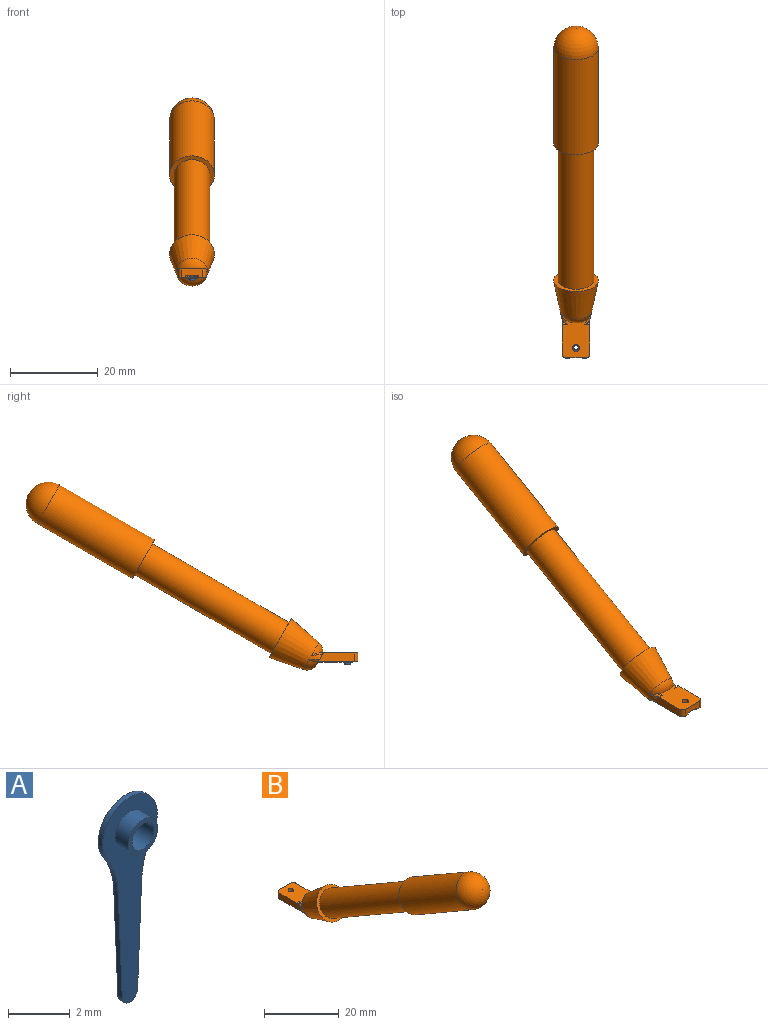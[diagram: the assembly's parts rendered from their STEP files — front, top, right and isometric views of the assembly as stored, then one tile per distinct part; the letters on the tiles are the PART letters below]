
ASSEMBLY  parts=2 mates=2
PART A: 11 faces, bbox 2.5x0.8x8.1 mm
  f0: cylinder r=0.68mm len=1.35mm, axis (0,1,0), area 2.5mm2, adj f1,f2
  f1: plane 1.35x1.35mm, normal (0,-1,0), area 0.6mm2, adj f0,f3
  f2: plane 8.1x2.5mm, normal (0,-1,0), area 8.8mm2, adj f0,f4,f5,f6,f7,f8,f9
  f3: cylinder r=0.5mm len=1mm, axis (0,-1,0), area 2.5mm2, adj f1,f10
  f4: plane 4.29x0.2mm, normal (1,0,-0.04), area 0.9mm2, adj f2,f5,f9,f10
  f5: cylinder r=3mm len=1.54mm, axis (0,-1,0), area 0.3mm2, adj f2,f4,f6,f10
  f6: cylinder r=1.25mm len=2.5mm, axis (0,-1,0), area 1.1mm2, adj f2,f5,f7,f10
  f7: cylinder r=3mm len=1.54mm, axis (0,-1,0), area 0.3mm2, adj f2,f6,f8,f10
  f8: plane 4.29x0.2mm, normal (-1,0,-0.04), area 0.9mm2, adj f2,f7,f9,f10
  f9: cylinder r=0.35mm len=0.7mm, axis (0,-1,0), area 0.2mm2, adj f2,f4,f8,f10
  f10: plane 8.1x2.5mm, normal (0,1,0), area 9.5mm2, adj f3,f4,f5,f6,f7,f8,f9
PART B: 37 faces, bbox 10.2x75.5x43.4 mm
  f0: plane 10.16x8.8mm, normal (0,-0.87,0.5), area 29.2mm2, adj f1,f6
  f1: cylinder r=4.06mm len=35.21mm, axis (0,-0.87,0.5), area 918.4mm2, adj f0,f2
  f2: plane 10.16x8.8mm, normal (0,0.87,-0.5), area 29.2mm2, adj f1,f3
  f3: cylinder r=5.08mm len=26.73mm, axis (0,-0.87,0.5), area 797.8mm2, adj f2,f28
  f4: plane 1.65x0.95mm, normal (0,-0.87,0.5), area 0.3mm2, adj f6,f24,f27,f33,f34,f35
  f5: plane 1.65x0.95mm, normal (0,-0.87,0.5), area 0.3mm2, adj f6,f22,f25,f31,f32,f36
  f6: cone r=3.17mm half-angle=10.6deg, axis (0,-0.87,0.5), area 228.7mm2, adj f0,f4,f5,f29,f30,f32,f34,f35
  f7: cylinder r=0.76mm len=1.52mm, axis (0,0,-1), area 6.7mm2, adj f14,f26
  f8: cylinder r=1.02mm len=1.91mm, axis (0,0,-1), area 2.5mm2, adj f19,f24,f26,f27
  f9: plane 2.26x0.51mm, normal (-1,0,0), area 1.1mm2, adj f10,f14,f19,f24
  f10: cylinder r=1.4mm len=0.88mm, axis (0,0,-1), area 0.5mm2, adj f9,f11,f14,f24
  f11: extruded ~1.41x0.53mm, area 0.8mm2, adj f10,f12,f14,f24
  f12: plane 4.1x0.51mm, normal (-1,0.03,0), area 2.1mm2, adj f11,f13,f14,f24
  f13: cylinder r=0.44mm len=0.51mm, axis (0,0,-1), area 0.1mm2, adj f12,f14,f23,f24
  f14: plane 8.7x2.79mm, normal (0,0,-1), area 13.2mm2, adj f7,f9,f10,f11,f12,f13,f15,f16
  f15: plane 4.1x0.51mm, normal (1,0.03,0), area 2.1mm2, adj f14,f16,f21,f22
  f16: extruded ~1.41x0.53mm, area 0.8mm2, adj f14,f15,f17,f22
  f17: cylinder r=1.4mm len=0.86mm, axis (0,0,-1), area 0.5mm2, adj f14,f16,f18,f22
  f18: plane 2.29x0.51mm, normal (1,0,0), area 1.2mm2, adj f14,f17,f19,f22
  f19: plane 4.62x1.91mm, normal (0,1,0), area 7.4mm2, adj f8,f9,f14,f18,f20,f22,f24,f26
  f20: cylinder r=1.02mm len=1.91mm, axis (0,0,-1), area 2.5mm2, adj f19,f22,f25,f26
  f21: cylinder r=0.44mm len=0.51mm, axis (0,0,-1), area 0.1mm2, adj f14,f15,f22,f23
  f22: plane 9.94x2.91mm, normal (0,0,-1), area 21.2mm2, adj f5,f15,f16,f17,f18,f19,f20,f21
  f23: plane 2.08x1.22mm, normal (0,0.87,-0.5), area 1.7mm2, adj f13,f14,f21,f22,f24,f29
  f24: plane 9.94x2.91mm, normal (0,0,-1), area 21.2mm2, adj f4,f8,f9,f10,f11,f12,f13,f19
  f25: plane 8.14x1.91mm, normal (-1,0,0), area 14.4mm2, adj f5,f20,f22,f26,f31
  f26: plane 8.87x6.35mm, normal (0,0,1), area 48.8mm2, adj f7,f8,f19,f20,f25,f27,f30,f31
  f27: plane 8.14x1.91mm, normal (1,0,0), area 14.4mm2, adj f4,f8,f24,f26,f33
  f28: sphere r=5.08mm, area 162.1mm2, adj f3
  f29: torus R=1.07mm, axis (0,0.87,-0.5), area 24.1mm2, adj f6,f22,f23,f24,f35,f36
  f30: torus R=1.07mm, axis (0,0.87,-0.5), area 16.9mm2, adj f6,f26,f32,f34
  f31: cylinder r=0.51mm len=1.23mm, axis (-1,0,0), area 0.5mm2, adj f5,f25,f26,f32
  f32: bspline ~4.94x2.3mm, area 1.3mm2, adj f5,f6,f26,f30,f31
  f33: cylinder r=0.51mm len=1.23mm, axis (-1,0,0), area 0.5mm2, adj f4,f26,f27,f34
  f34: bspline ~4.94x2.3mm, area 1.3mm2, adj f4,f6,f26,f30,f33
  f35: bspline ~3.78x0.94mm, area 1.2mm2, adj f4,f6,f24,f29
  f36: bspline ~3.78x0.94mm, area 1.2mm2, adj f5,f6,f22,f29
PLACE A rot(axis=(1,0,0),90deg) t=(0.67,-10.54,-2.96)mm
PLACE B rot(axis=(0,0,1),180deg) t=(0.67,-12.92,-2.76)mm
MATE cylindrical B.f13 <-> B.f7  axis (0,0,-1) through (0.67,-4.29,-2.76)mm
MATE planar A.f10 <-> B.f22  axis (0,0,1) through (1.71,-9.84,-2.76)mm
